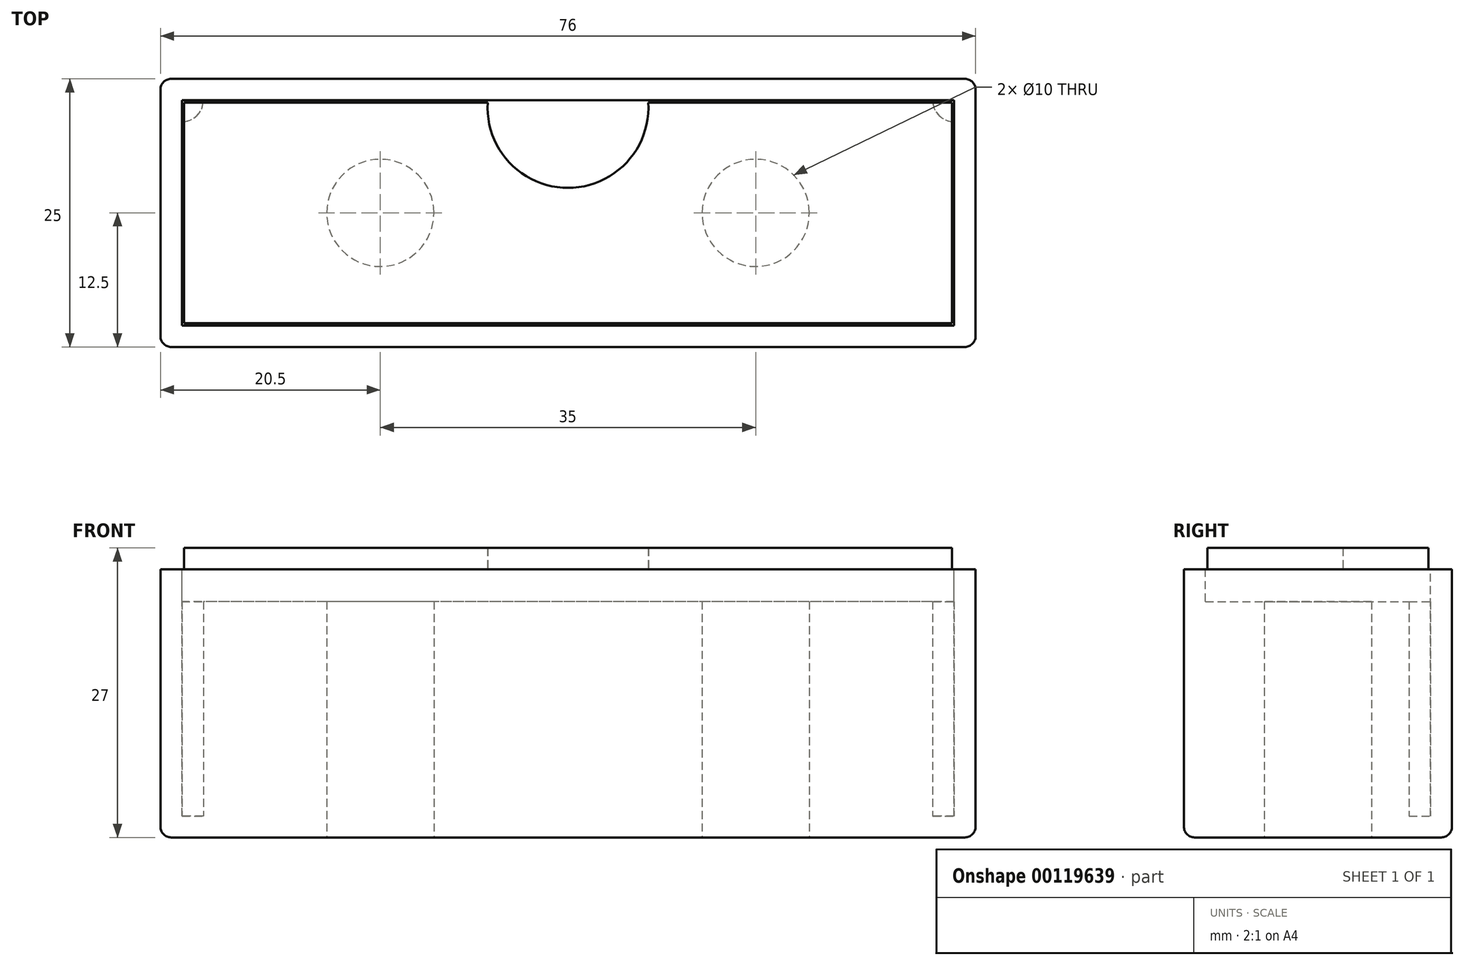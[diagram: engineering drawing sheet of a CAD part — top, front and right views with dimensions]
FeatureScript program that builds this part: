
annotation { "Feature Type Name" : "Feature", "Feature Type Description" : "" }
export const myFeature = defineFeature(function(context is Context, id is Id, definition is map)
    precondition{}
    {
        {
            var Q0;
            Q0=qCreatedBy(makeId("Top.planeOp"),FACE);
            var sketch = newSketch(context, id + "F0", { "sketchPlane" : qUnion([Q0])});
            skCircle(sketch, "E0", {"center": v(-17.5, 0) * mm, "radius": 5 * mm});
            skLineSegment(sketch, "E1.bottom", {"start": v(-5, -7.5) * mm, "end": v(-30, -7.5) * mm, "construction": true});
            skLineSegment(sketch, "E1.top", {"start": v(-5, 7.5) * mm, "end": v(-30, 7.5) * mm, "construction": true});
            skLineSegment(sketch, "E1.left", {"start": v(-5, -7.5) * mm, "end": v(-5, 7.5) * mm, "construction": true});
            skLineSegment(sketch, "E1.right", {"start": v(-30, -7.5) * mm, "end": v(-30, 7.5) * mm, "construction": true});
            skCircle(sketch, "E2.MirrorC", {"center": v(17.5, 0) * mm, "radius": 5 * mm});
            skLineSegment(sketch, "E3.bottom", {"start": v(38, -12.5) * mm, "end": v(-38, -12.5) * mm});
            skLineSegment(sketch, "E3.top", {"start": v(38, 12.5) * mm, "end": v(-38, 12.5) * mm});
            skLineSegment(sketch, "E3.left", {"start": v(38, -12.5) * mm, "end": v(38, 12.5) * mm});
            skLineSegment(sketch, "E3.right", {"start": v(-38, -12.5) * mm, "end": v(-38, 12.5) * mm});
            skPoint(sketch, "E3.middle", {"position": v(0, 0) * mm});
            skSolve(sketch);
        }
        {
            var Q0;
            Q0=makeQuery(id+"F0.imprint","IMPRINT",FACE,{"disambiguationData":[TD([[makeQuery(id+"F0.imprint","IMPRINT",EDGE,{"derivedFrom":sQuery(id+"F0.wireOp",EDGE,"E0")}),-1.0]])]});
            extrude(context, id + "F1", {"entities" : qUnion([Q0]), "depth" : 25 * mm});
        }
        {
            var Q0;
            Q0=makeQuery(id+"F1.opExtrude","CAP_FACE",FACE,{"disambiguationData":[OSD([sQuery(id+"F0.wireOp",EDGE,"E0"),sQuery(id+"F0.wireOp",EDGE,"E2.MirrorC"),sQuery(id+"F0.wireOp",EDGE,"E3.bottom"),sQuery(id+"F0.wireOp",EDGE,"E3.top"),sQuery(id+"F0.wireOp",EDGE,"E3.left"),sQuery(id+"F0.wireOp",EDGE,"E3.right")])],"isStart":false});
            var sketch = newSketch(context, id + "F2", { "sketchPlane" : qUnion([Q0])});
            skLineSegment(sketch, "E4.bottom", {"start": v(36, -10.5) * mm, "end": v(-36, -10.5) * mm});
            skLineSegment(sketch, "E4.top", {"start": v(36, 10.5) * mm, "end": v(-36, 10.5) * mm});
            skLineSegment(sketch, "E4.left", {"start": v(36, -10.5) * mm, "end": v(36, 10.5) * mm});
            skLineSegment(sketch, "E4.right", {"start": v(-36, -10.5) * mm, "end": v(-36, 10.5) * mm});
            skPoint(sketch, "E4.middle", {"position": v(0, 0) * mm});
            skSolve(sketch);
        }
        {
            var Q0;
            Q0=makeQuery(id+"F2.imprint","IMPRINT",FACE,{"disambiguationData":[TD([[makeQuery(id+"F2.imprint","IMPRINT",EDGE,{"derivedFrom":sQuery(id+"F2.wireOp",EDGE,"E4.bottom")}),-1.0]])]});
            extrude(context, id + "F3", {"entities" : qUnion([Q0]), "operationType" : NewBodyOperationType.REMOVE, "oppositeDirection" : true, "depth" : 23 * mm});
        }
        {
            var Q0;
            Q0=makeQuery(id+"F3.boolean.opBoolean","COPY",FACE,{"derivedFrom":makeQuery(id+"F3.opExtrude","CAP_FACE",FACE,{"disambiguationData":[OSD([sQuery(id+"F0.wireOp",EDGE,"E0"),sQuery(id+"F0.wireOp",EDGE,"E2.MirrorC"),sQuery(id+"F2.wireOp",EDGE,"E4.bottom"),sQuery(id+"F2.wireOp",EDGE,"E4.top"),sQuery(id+"F2.wireOp",EDGE,"E4.left"),sQuery(id+"F2.wireOp",EDGE,"E4.right")])],"isStart":false})});
            var sketch = newSketch(context, id + "F4", { "sketchPlane" : qUnion([Q0])});
            skArc(sketch, "E5", {"start": v(-34, 10.5) * mm, "mid": v(-34.59, 9.09) * mm, "end": v(-36, 8.5) * mm});
            skArc(sketch, "E6", {"start": v(-34, -10.5) * mm, "mid": v(-34.59, -9.09) * mm, "end": v(-36, -8.5) * mm});
            skArc(sketch, "E7", {"start": v(36, -8.5) * mm, "mid": v(34.59, -9.09) * mm, "end": v(34, -10.5) * mm});
            skArc(sketch, "E8", {"start": v(36, 8.5) * mm, "mid": v(34.59, 9.09) * mm, "end": v(34, 10.5) * mm});
            skSolve(sketch);
        }
        {
            var Q0;
            Q0=makeQuery(id+"F1.opExtrude","CAP_FACE",FACE,{"disambiguationData":[OSD([sQuery(id+"F0.wireOp",EDGE,"E0"),sQuery(id+"F0.wireOp",EDGE,"E2.MirrorC"),sQuery(id+"F0.wireOp",EDGE,"E3.bottom"),sQuery(id+"F0.wireOp",EDGE,"E3.top"),sQuery(id+"F0.wireOp",EDGE,"E3.left"),sQuery(id+"F0.wireOp",EDGE,"E3.right")])],"isStart":false});
            var sketch = newSketch(context, id + "F5", { "sketchPlane" : qUnion([Q0])});
            skLineSegment(sketch, "E9.bottom", {"start": v(35.8, -10.3) * mm, "end": v(-35.8, -10.3) * mm});
            skLineSegment(sketch, "E9.top", {"start": v(35.8, 10.3) * mm, "end": v(-35.8, 10.3) * mm});
            skLineSegment(sketch, "E9.left", {"start": v(35.8, -10.3) * mm, "end": v(35.8, 10.3) * mm});
            skLineSegment(sketch, "E9.right", {"start": v(-35.8, -10.3) * mm, "end": v(-35.8, 10.3) * mm});
            skPoint(sketch, "E9.middle", {"position": v(0, 0) * mm});
            skCircle(sketch, "E10", {"center": v(0, 9.84) * mm, "radius": 7.5 * mm});
            skPoint(sketch, "E10.centerSnap0", {"position": v(0, 10.3) * mm});
            skSolve(sketch);
        }
        {
            var Q0;
            Q0=makeQuery(id+"F5.imprint","IMPRINT",FACE,{"disambiguationData":[TD([[makeQuery(id+"F5.imprint","IMPRINT",EDGE,{"derivedFrom":sQuery(id+"F5.wireOp",EDGE,"E9.bottom")}),-1.0]])]});
            extrude(context, id + "F6", {"entities" : qUnion([Q0]), "depth" : 2 * mm});
        }
        {
            var Q0;
            Q0=makeQuery(id+"F1.opExtrude","CAP_EDGE",EDGE,{"disambiguationData":[OSD([sQuery(id+"F0.wireOp",EDGE,"E3.left")])],"isStart":true});
            var Q1;
            Q1=makeQuery(id+"F1.opExtrude","CAP_EDGE",EDGE,{"disambiguationData":[OSD([sQuery(id+"F0.wireOp",EDGE,"E3.bottom")])],"isStart":true});
            var Q2;
            Q2=makeQuery(id+"F1.opExtrude","CAP_EDGE",EDGE,{"disambiguationData":[OSD([sQuery(id+"F0.wireOp",EDGE,"E3.right")])],"isStart":true});
            var Q3;
            Q3=makeQuery(id+"F1.opExtrude","SWEPT_EDGE",EDGE,{"disambiguationData":[OSD([sQuery(id+"F0.wireOp",EDGE,"E3.bottom"),sQuery(id+"F0.wireOp",EDGE,"E3.left")])]});
            var Q4;
            Q4=makeQuery(id+"F1.opExtrude","SWEPT_EDGE",EDGE,{"disambiguationData":[OSD([sQuery(id+"F0.wireOp",EDGE,"E3.bottom"),sQuery(id+"F0.wireOp",EDGE,"E3.right")])]});
            var Q5;
            Q5=makeQuery(id+"F1.opExtrude","SWEPT_EDGE",EDGE,{"disambiguationData":[OSD([sQuery(id+"F0.wireOp",EDGE,"E3.top"),sQuery(id+"F0.wireOp",EDGE,"E3.left")])]});
            var Q6;
            Q6=makeQuery(id+"F1.opExtrude","SWEPT_EDGE",EDGE,{"disambiguationData":[OSD([sQuery(id+"F0.wireOp",EDGE,"E3.top"),sQuery(id+"F0.wireOp",EDGE,"E3.right")])]});
            var Q7;
            Q7=makeQuery(id+"F1.opExtrude","CAP_EDGE",EDGE,{"disambiguationData":[OSD([sQuery(id+"F0.wireOp",EDGE,"E3.top")])],"isStart":true});
            fillet(context, id + "F7", {"entities" : qUnion([Q0, Q1, Q2, Q3, Q4, Q5, Q6, Q7]), "radius" : 1 * mm, "tangentPropagation" : true, "allowEdgeOverflow" : false});
        }
        {
            var Q0;
            {var subQ0=sQuery(id+"F4.wireOp",EDGE,"E5");Q0=makeQuery(id+"F4.imprint","IMPRINT",FACE,{"disambiguationData":[TD([[makeQuery(id+"F4.imprint","IMPRINT",EDGE,{"derivedFrom":subQ0}),-1.0]])]});}
            var Q1;
            {var subQ0=sQuery(id+"F4.wireOp",EDGE,"E6");Q1=makeQuery(id+"F4.imprint","IMPRINT",FACE,{"disambiguationData":[TD([[makeQuery(id+"F4.imprint","IMPRINT",EDGE,{"derivedFrom":subQ0}),1.0]])]});}
            var Q2;
            {var subQ0=sQuery(id+"F4.wireOp",EDGE,"E7");Q2=makeQuery(id+"F4.imprint","IMPRINT",FACE,{"disambiguationData":[TD([[makeQuery(id+"F4.imprint","IMPRINT",EDGE,{"derivedFrom":subQ0}),1.0]])]});}
            var Q3;
            {var subQ0=sQuery(id+"F4.wireOp",EDGE,"E8");Q3=makeQuery(id+"F4.imprint","IMPRINT",FACE,{"disambiguationData":[TD([[makeQuery(id+"F4.imprint","IMPRINT",EDGE,{"derivedFrom":subQ0}),-1.0]])]});}
            extrude(context, id + "F8", {"entities" : qUnion([Q0, Q1, Q2, Q3]), "operationType" : NewBodyOperationType.ADD, "depth" : 20 * mm, "hasSecondDirection" : true, "secondDirectionOppositeDirection" : true, "secondDirectionDepth" : 1 * mm});
        }
    });
